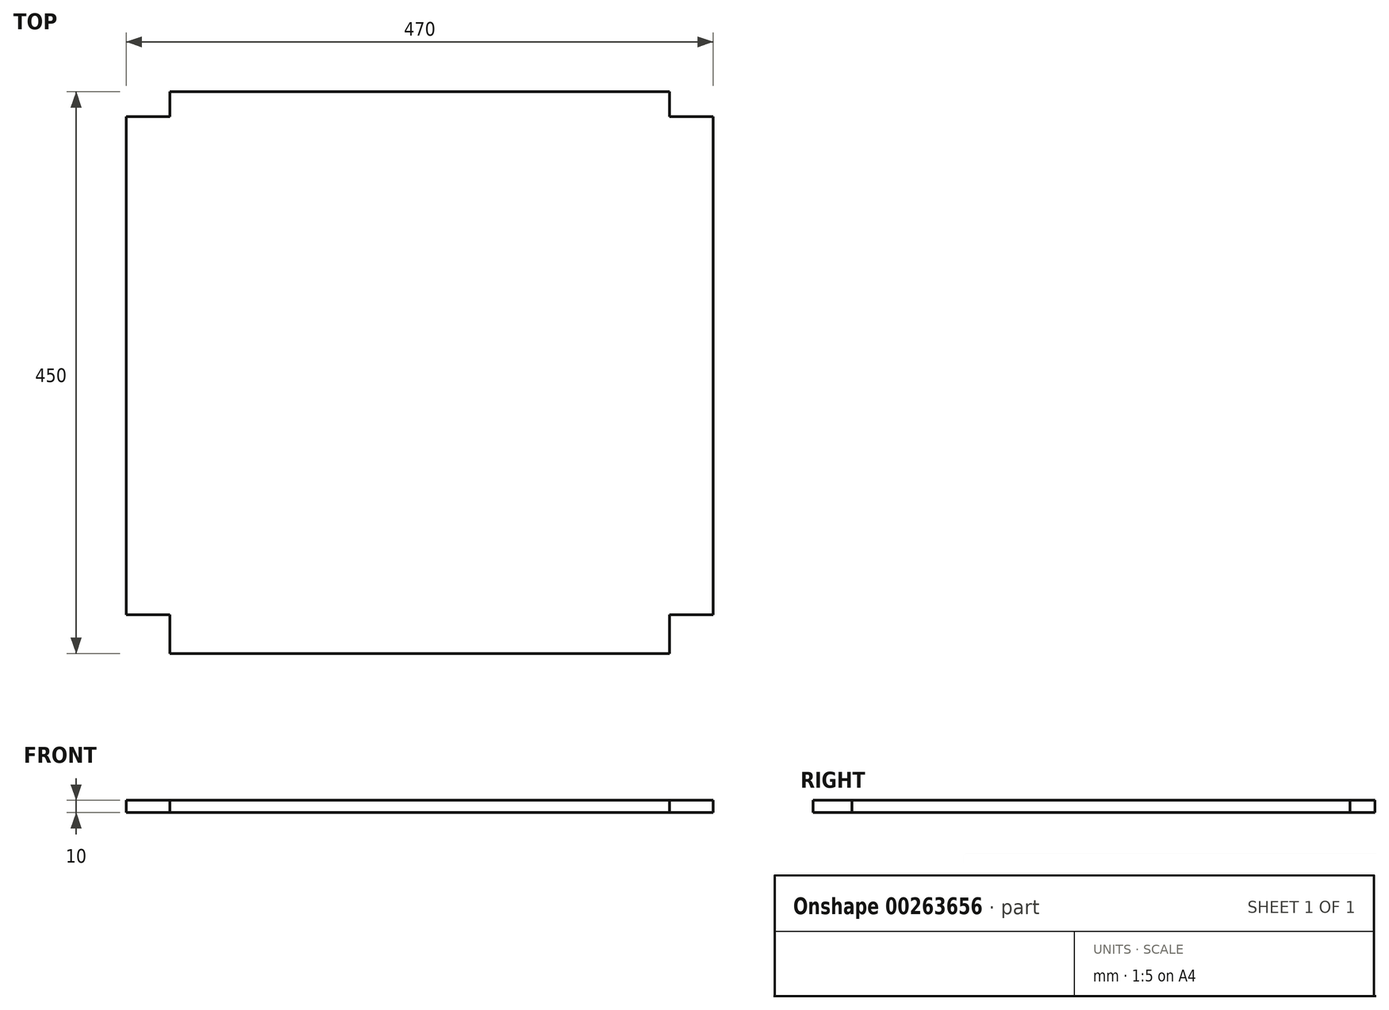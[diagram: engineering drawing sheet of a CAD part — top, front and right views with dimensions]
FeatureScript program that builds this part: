
annotation { "Feature Type Name" : "Feature", "Feature Type Description" : "" }
export const myFeature = defineFeature(function(context is Context, id is Id, definition is map)
    precondition{}
    {
        {
            var Q0;
            Q0=qCreatedBy(makeId("Top.planeOp"),FACE);
            var sketch = newSketch(context, id + "F0", { "sketchPlane" : qUnion([Q0])});
            skLineSegment(sketch, "E0", {"start": v(0, 0) * mm, "end": v(470, 0) * mm});
            skLineSegment(sketch, "E1", {"start": v(470, 0) * mm, "end": v(470, 450) * mm});
            skLineSegment(sketch, "E2", {"start": v(470, 450) * mm, "end": v(0, 450) * mm});
            skLineSegment(sketch, "E3", {"start": v(0, 450) * mm, "end": v(0, 0) * mm});
            skSolve(sketch);
        }
        {
            var Q0;
            Q0=qSketchRegion(id+"F0",true);
            extrude(context, id + "F1", {"entities" : qUnion([Q0]), "depth" : 10 * mm});
        }
        {
            var Q0;
            Q0=makeQuery(id+"F1.opExtrude","CAP_FACE",FACE,{"disambiguationData":[OSD([sQuery(id+"F0.wireOp",EDGE,"E0"),sQuery(id+"F0.wireOp",EDGE,"E1"),sQuery(id+"F0.wireOp",EDGE,"E2"),sQuery(id+"F0.wireOp",EDGE,"E3")])],"isStart":false});
            var sketch = newSketch(context, id + "F2", { "sketchPlane" : qUnion([Q0])});
            skLineSegment(sketch, "E4.bottom", {"start": v(35, 450) * mm, "end": v(0, 450) * mm});
            skLineSegment(sketch, "E4.top", {"start": v(35, 430) * mm, "end": v(0, 430) * mm});
            skLineSegment(sketch, "E4.left", {"start": v(35, 450) * mm, "end": v(35, 430) * mm});
            skLineSegment(sketch, "E4.right", {"start": v(0, 450) * mm, "end": v(0, 430) * mm});
            skLineSegment(sketch, "E5.bottom", {"start": v(0, 0) * mm, "end": v(35, 0) * mm});
            skLineSegment(sketch, "E5.top", {"start": v(0, 31) * mm, "end": v(35, 31) * mm});
            skLineSegment(sketch, "E5.left", {"start": v(0, 0) * mm, "end": v(0, 31) * mm});
            skLineSegment(sketch, "E5.right", {"start": v(35, 0) * mm, "end": v(35, 31) * mm});
            skLineSegment(sketch, "E6", {"start": v(235, 450) * mm, "end": v(235, 0) * mm, "construction": true});
            skLineSegment(sketch, "E7.MirrorCS", {"start": v(470, 450) * mm, "end": v(470, 430) * mm});
            skLineSegment(sketch, "E8.MirrorCS", {"start": v(435, 450) * mm, "end": v(470, 450) * mm});
            skLineSegment(sketch, "E9.MirrorCS", {"start": v(435, 430) * mm, "end": v(470, 430) * mm});
            skLineSegment(sketch, "E10.MirrorCS", {"start": v(435, 450) * mm, "end": v(435, 430) * mm});
            skLineSegment(sketch, "E11.MirrorCS", {"start": v(470, 31) * mm, "end": v(435, 31) * mm});
            skLineSegment(sketch, "E12.MirrorCS", {"start": v(470, 0) * mm, "end": v(435, 0) * mm});
            skLineSegment(sketch, "E13.MirrorCS", {"start": v(435, 0) * mm, "end": v(435, 31) * mm});
            skLineSegment(sketch, "E14.MirrorCS", {"start": v(470, 0) * mm, "end": v(470, 31) * mm});
            skSolve(sketch);
        }
        {
            var Q0;
            Q0=qSketchRegion(id+"F2",true);
            extrude(context, id + "F3", {"entities" : qUnion([Q0]), "operationType" : NewBodyOperationType.REMOVE, "endBound" : BoundingType.THROUGH_ALL, "oppositeDirection" : true, "depth" : 25 * mm});
        }
    });
